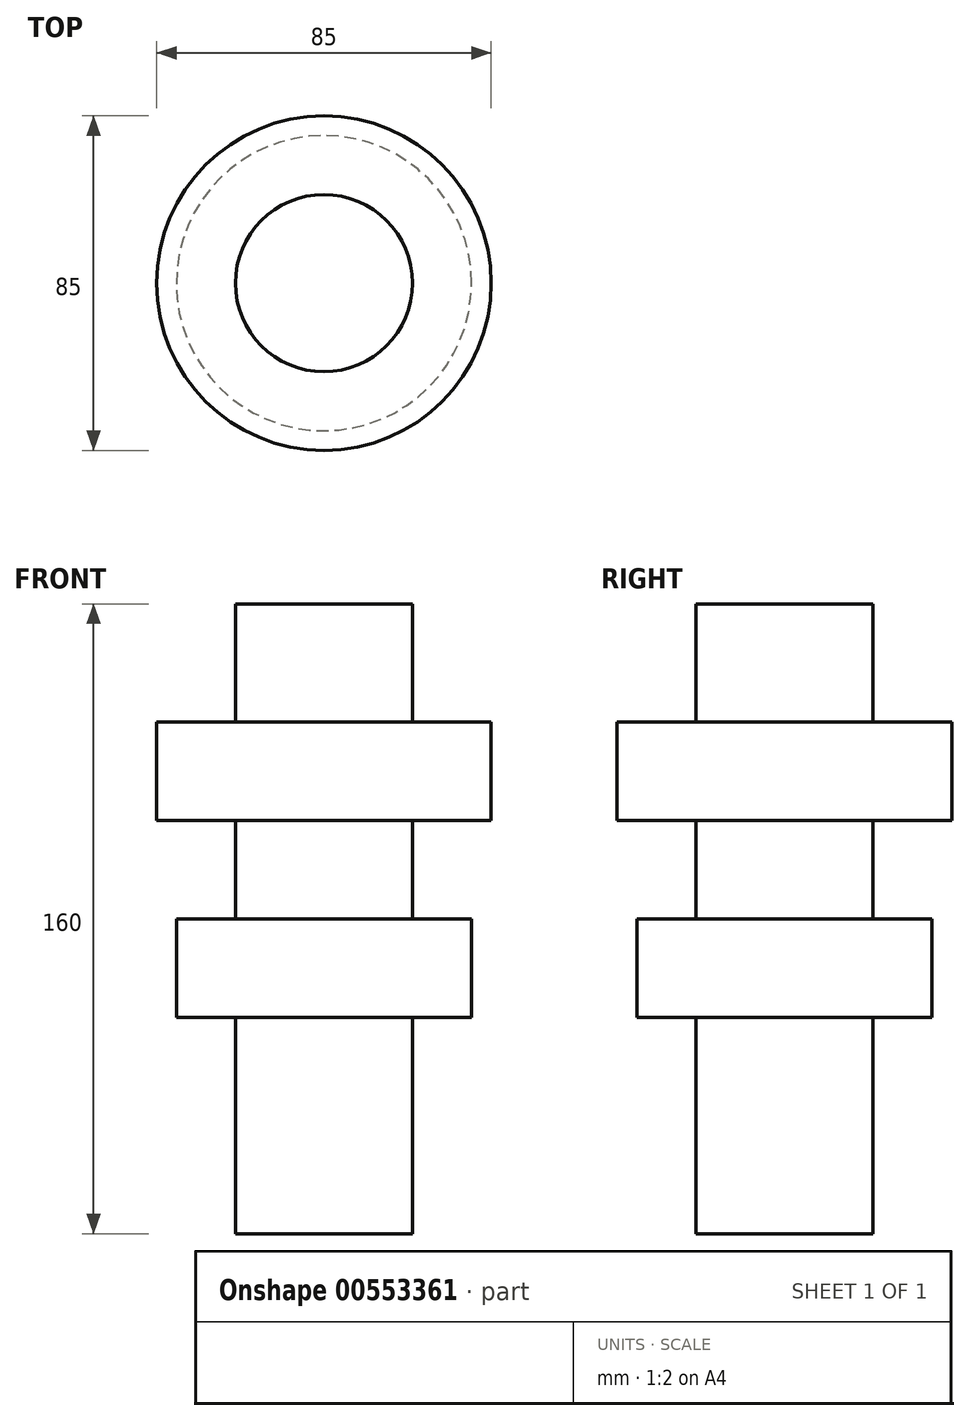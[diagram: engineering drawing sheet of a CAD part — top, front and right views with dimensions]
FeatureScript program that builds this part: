
annotation { "Feature Type Name" : "Feature", "Feature Type Description" : "" }
export const myFeature = defineFeature(function(context is Context, id is Id, definition is map)
    precondition{}
    {
        {
            var Q0;
            Q0=qCreatedBy(makeId("Top.planeOp"),FACE);
            var sketch = newSketch(context, id + "F0", { "sketchPlane" : qUnion([Q0])});
            skCircle(sketch, "E0", {"center": v(0, 0) * mm, "radius": 37.5 * mm});
            skSolve(sketch);
        }
        {
            var Q0;
            Q0=makeQuery(id+"F0.imprint","IMPRINT",FACE,{"disambiguationData":[TD([[makeQuery(id+"F0.imprint","IMPRINT",EDGE,{"derivedFrom":sQuery(id+"F0.wireOp",EDGE,"E0")}),1.0]])]});
            extrude(context, id + "F1", {"entities" : qUnion([Q0]), "depth" : 25 * mm, "offsetDistance" : 25 * mm});
        }
        {
            var Q0;
            Q0=makeQuery(id+"F1.opExtrude","CAP_FACE",FACE,{"disambiguationData":[OSD([sQuery(id+"F0.wireOp",EDGE,"E0")])],"isStart":false});
            var sketch = newSketch(context, id + "F2", { "sketchPlane" : qUnion([Q0])});
            skCircle(sketch, "E1", {"center": v(0, 0) * mm, "radius": 22.5 * mm});
            skSolve(sketch);
        }
        {
            var Q0;
            Q0=makeQuery(id+"F2.imprint","IMPRINT",FACE,{"disambiguationData":[TD([[makeQuery(id+"F2.imprint","IMPRINT",EDGE,{"derivedFrom":sQuery(id+"F2.wireOp",EDGE,"E1")}),1.0]])]});
            extrude(context, id + "F3", {"entities" : qUnion([Q0]), "operationType" : NewBodyOperationType.ADD, "oppositeDirection" : true, "depth" : 80 * mm, "offsetDistance" : 25 * mm, "hasSecondDirection" : true, "secondDirectionOppositeDirection" : false, "secondDirectionDepth" : 80 * mm});
        }
        {
            var Q0;
            Q0=makeQuery(id+"F1.opExtrude","CAP_FACE",FACE,{"disambiguationData":[OSD([sQuery(id+"F0.wireOp",EDGE,"E0")])],"isStart":false});
            var sketch = newSketch(context, id + "F4", { "sketchPlane" : qUnion([Q0])});
            skCircle(sketch, "E2", {"center": v(0, 0) * mm, "radius": 42.5 * mm});
            skSolve(sketch);
        }
        {
            var Q0;
            Q0 = qSketchRegion(id + "F4", true);
            extrude(context, id + "F5", {"entities" : qUnion([Q0]), "operationType" : NewBodyOperationType.ADD, "depth" : 50 * mm, "offsetDistance" : 25 * mm, "hasSecondDirection" : true, "secondDirectionOppositeDirection" : false, "secondDirectionDepth" : 25 * mm});
        }
    });
